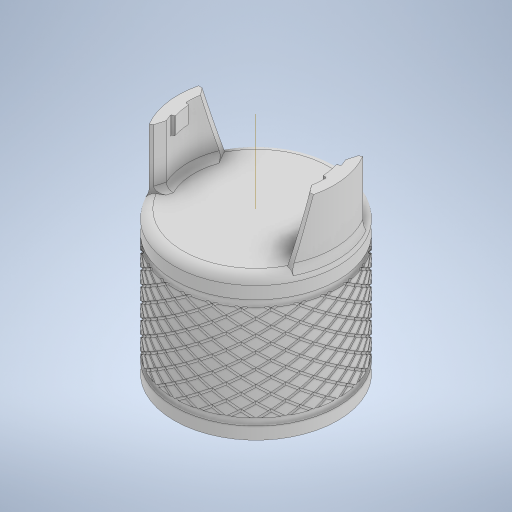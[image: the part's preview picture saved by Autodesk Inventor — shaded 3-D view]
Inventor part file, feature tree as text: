
AUTODESK INVENTOR PART (.ipt)
format: ipt  version: 2023 (Build 270158030, 158C)  size: 3,565,568 bytes
history: native  units: mm
features: sketch x7, projected_geometry x6, extrude x5, fillet x3, chamfer x2, pattern_circular x2, plane x1, revolve x1, helix x1, mirror x1
ambient origin geometry x8: Origin, YZ Plane, XZ Plane, XY Plane, X Axis, Y Axis, Z Axis, Center Point
bodies: Solid1 (feature_tree)
feature tree (29):
  extrude  "Extrusion1"  Depth=16.3mm TaperAngle=0.0deg
  extrude  "tooth"  Depth=7.8mm
  extrude  "Extrusion3"  Depth=6.8mm TaperAngle=0.0deg
  chamfer  "Chamfer1"  Distance=2.0mm
  plane  "Work Plane2"
  extrude  "Extrusion4"  Depth=2.0mm
  chamfer  "Chamfer2"  Distance=20.0mm
  fillet  "Fillet1"  Radius=0.7mm
  pattern_circular  "Circular Pattern1"  Count=2 Angle=360.0deg
  extrude  "rod-insertion"  Depth=2.0mm
  fillet  "Fillet2"  Radius=3.535mm
  revolve  "Revolution1"  [1 undecoded]
  helix  "Coil1"  [1 undecoded]
  mirror  "Mirror1"
  pattern_circular  "Circular Pattern2"  [2 undecoded]
  fillet  "Fillet3"  Radius=1.0mm
  sketch  "Sketch1"  dims[d0=18.7mm d1=16.3mm d2=0.0mm]
  sketch  "Sketch2"  dims[d3=1.6mm d4=7.8mm]
  projected_geometry  "Projected Loop1"
  sketch  "Sketch4"  dims[d5=3.9mm d6=6.8mm d7=0.0mm]
  projected_geometry  "Projected Loop2"
  sketch  "Sketch6"  dims[d8=1.7mm]
  projected_geometry  "Projected Loop3"
  projected_geometry  "Projected Loop4"
  sketch  "Sketch7"  dims[d9=2.0mm d12=2.0mm d13=0.0mm]
  sketch  "Sketch8"  dims[d14=0.08mm d15=2.0mm d16=45.0deg d17=6.0mm d18=20.0mm d19=0.0mm]
  projected_geometry  "Projected Loop5"
  sketch  "Sketch9"  dims[d20=0.8mm d21=2.0mm d22=45.0deg d23=0.7mm d24=20.0mm d25=360.0deg d27=7.07mm d28=3.535mm d29=10.0mm d30=3.5mm d31=7.0mm d32=12.5mm d33=0.0mm d34=1.0mm d35=1.8mm d36=1.8mm d37=0.8mm d38=9.35mm d39=9.35mm d40=90.0deg d41=0.3mm d42=9.35mm d45=40.0mm d46=11.5mm d47=20.0mm d48=0.0mm d49=90.0deg d50=90.0deg d51=0.0mm d52=0.0mm d53=10.9mm d54=0.15mm d55=240.0mm d56=360.0deg d58=1.172702mm d59=0.4mm d60=2.0mm]
  projected_geometry  "Projected Loop6"
note: 4 required parameter values undecoded (feature->parameter linkage not recoverable at this tier; creation-order binding heuristic only, values carry confidence <= 0.55)